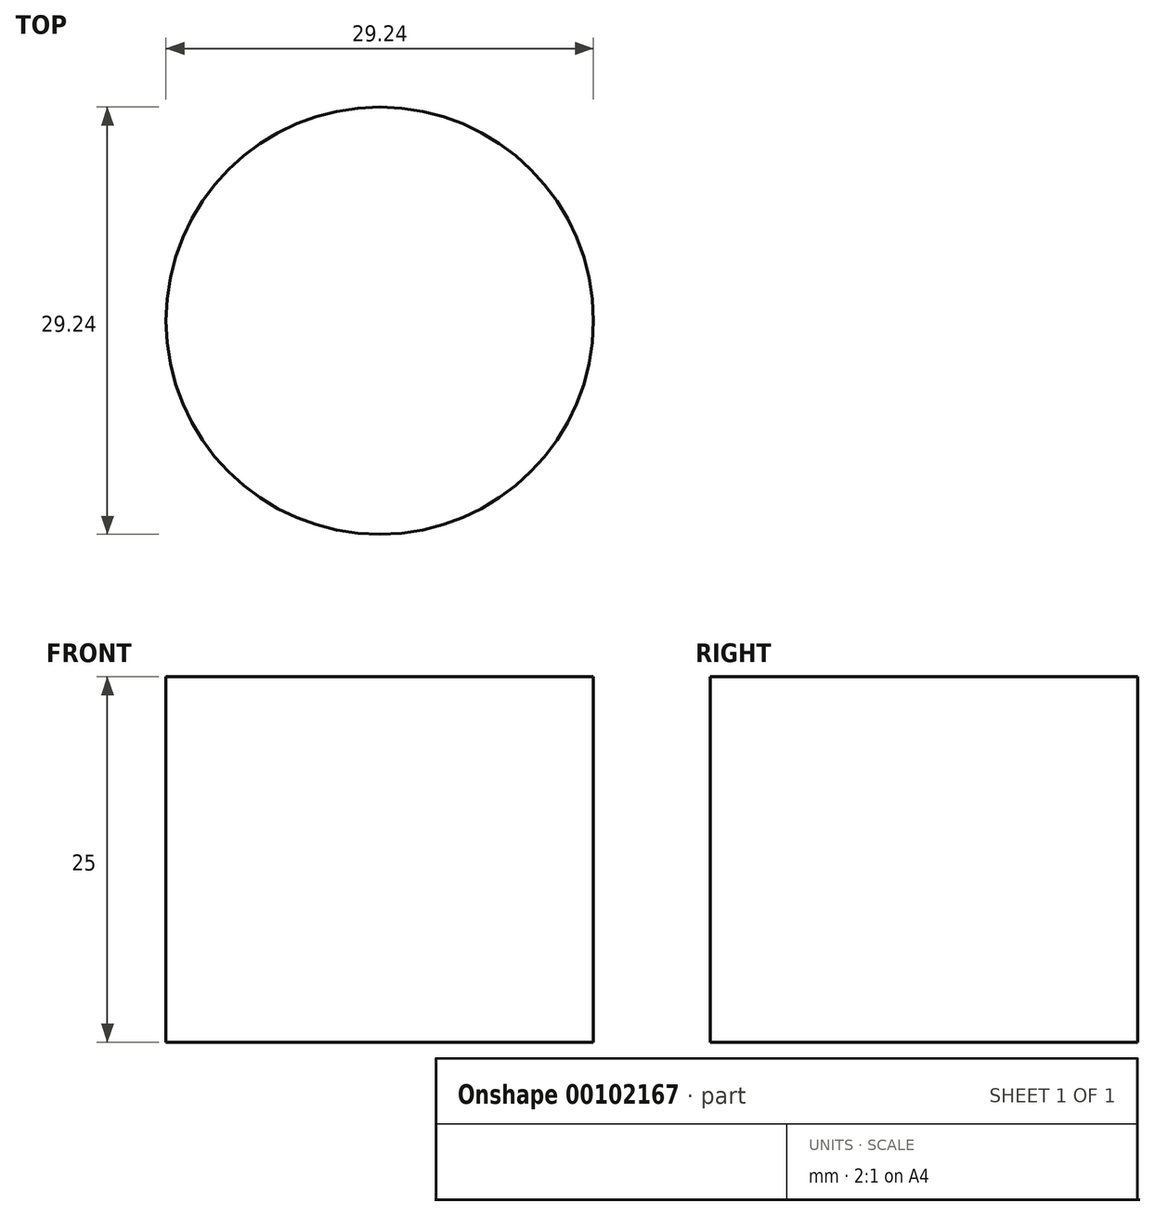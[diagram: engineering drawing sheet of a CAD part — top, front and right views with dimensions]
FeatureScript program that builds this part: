
annotation { "Feature Type Name" : "Feature", "Feature Type Description" : "" }
export const myFeature = defineFeature(function(context is Context, id is Id, definition is map)
    precondition{}
    {
        {
            var Q0;
            Q0=qCreatedBy(makeId("Top.planeOp"),FACE);
            var sketch = newSketch(context, id + "F0", { "sketchPlane" : qUnion([Q0])});
            skCircle(sketch, "E0", {"center": v(-45.65, 32.3) * mm, "radius": 14.62 * mm});
            skSolve(sketch);
        }
        {
            var Q0;
            Q0=makeQuery(id+"F0.imprint","IMPRINT",FACE,{"disambiguationData":[TD([[makeQuery(id+"F0.imprint","IMPRINT",EDGE,{"derivedFrom":sQuery(id+"F0.wireOp",EDGE,"E0")}),1.0]])]});
            extrude(context, id + "F1", {"entities" : qUnion([Q0]), "depth" : 25 * mm});
        }
    });
